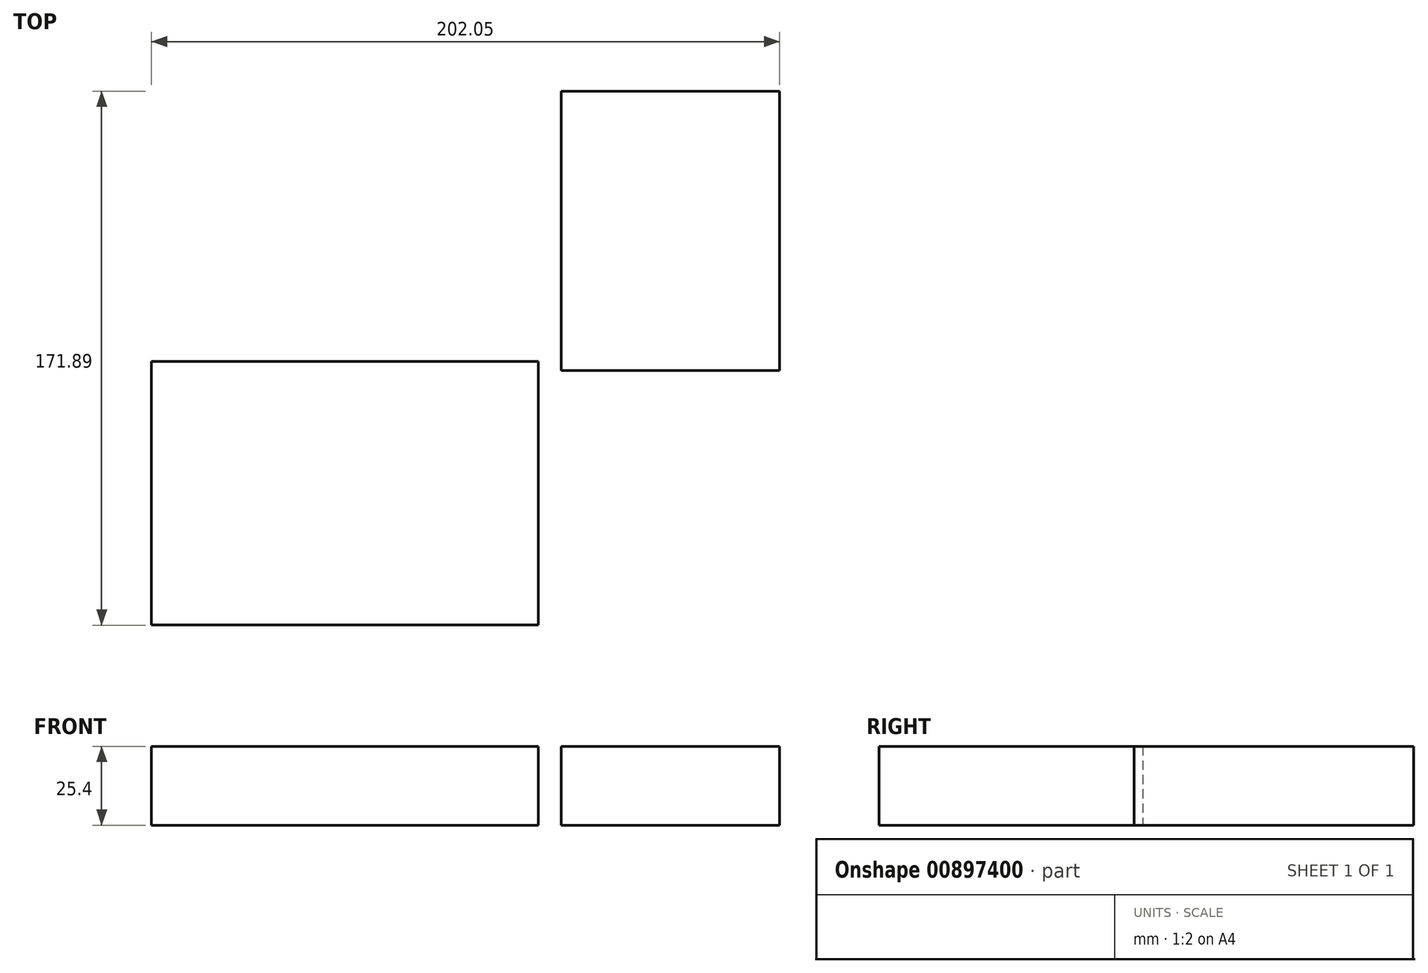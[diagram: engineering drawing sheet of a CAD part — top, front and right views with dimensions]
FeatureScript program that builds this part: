
annotation { "Feature Type Name" : "Feature", "Feature Type Description" : "" }
export const myFeature = defineFeature(function(context is Context, id is Id, definition is map)
    precondition{}
    {
        {
            var Q0;
            Q0=qCreatedBy(makeId("Top.planeOp"),FACE);
            var sketch = newSketch(context, id + "F0", { "sketchPlane" : qUnion([Q0])});
            skLineSegment(sketch, "E0.bottom", {"start": v(-53.84, -14.12) * mm, "end": v(16.44, -14.12) * mm});
            skLineSegment(sketch, "E0.top", {"start": v(-53.84, 50.35) * mm, "end": v(16.44, 50.35) * mm});
            skLineSegment(sketch, "E0.left", {"start": v(-53.84, -14.12) * mm, "end": v(-53.84, 50.35) * mm});
            skLineSegment(sketch, "E0.right", {"start": v(16.44, -14.12) * mm, "end": v(16.44, 50.35) * mm});
            skSolve(sketch);
        }
        {
            var Q0;
            Q0=makeQuery(id+"F0.imprint","IMPRINT",FACE,{"disambiguationData":[TD([[makeQuery(id+"F0.imprint","IMPRINT",EDGE,{"derivedFrom":sQuery(id+"F0.wireOp",EDGE,"E0.bottom")}),1.0]])]});
            extrude(context, id + "F1", {"entities" : qUnion([Q0]), "depth" : 25.4 * mm, "offsetDistance" : 25.4 * mm});
        }
        {
            var Q0;
            Q0=makeQuery(id+"F1.opExtrude","SWEPT_FACE",FACE,{"disambiguationData":[OSD([sQuery(id+"F0.wireOp",EDGE,"E0.bottom")])]});
            extrude(context, id + "F2", {"entities" : qUnion([Q0]), "operationType" : NewBodyOperationType.ADD, "depth" : 25.4 * mm, "offsetDistance" : 25.4 * mm});
        }
        {
            var Q0;
            Q0=qCreatedBy(makeId("Top.planeOp"),FACE);
            var sketch = newSketch(context, id + "F3", { "sketchPlane" : qUnion([Q0])});
            skLineSegment(sketch, "E1.bottom", {"start": v(-185.6, -36.68) * mm, "end": v(-61.12, -36.68) * mm});
            skLineSegment(sketch, "E1.top", {"start": v(-185.6, -121.54) * mm, "end": v(-61.12, -121.54) * mm});
            skLineSegment(sketch, "E1.left", {"start": v(-185.6, -36.68) * mm, "end": v(-185.6, -121.54) * mm});
            skLineSegment(sketch, "E1.right", {"start": v(-61.12, -36.68) * mm, "end": v(-61.12, -121.54) * mm});
            skSolve(sketch);
        }
        {
            var Q0;
            Q0=makeQuery(id+"F3.imprint","IMPRINT",FACE,{"disambiguationData":[TD([[makeQuery(id+"F3.imprint","IMPRINT",EDGE,{"derivedFrom":sQuery(id+"F3.wireOp",EDGE,"E1.bottom")}),-1.0]])]});
            extrude(context, id + "F4", {"entities" : qUnion([Q0]), "depth" : 25.4 * mm, "offsetDistance" : 25.4 * mm});
        }
    });
